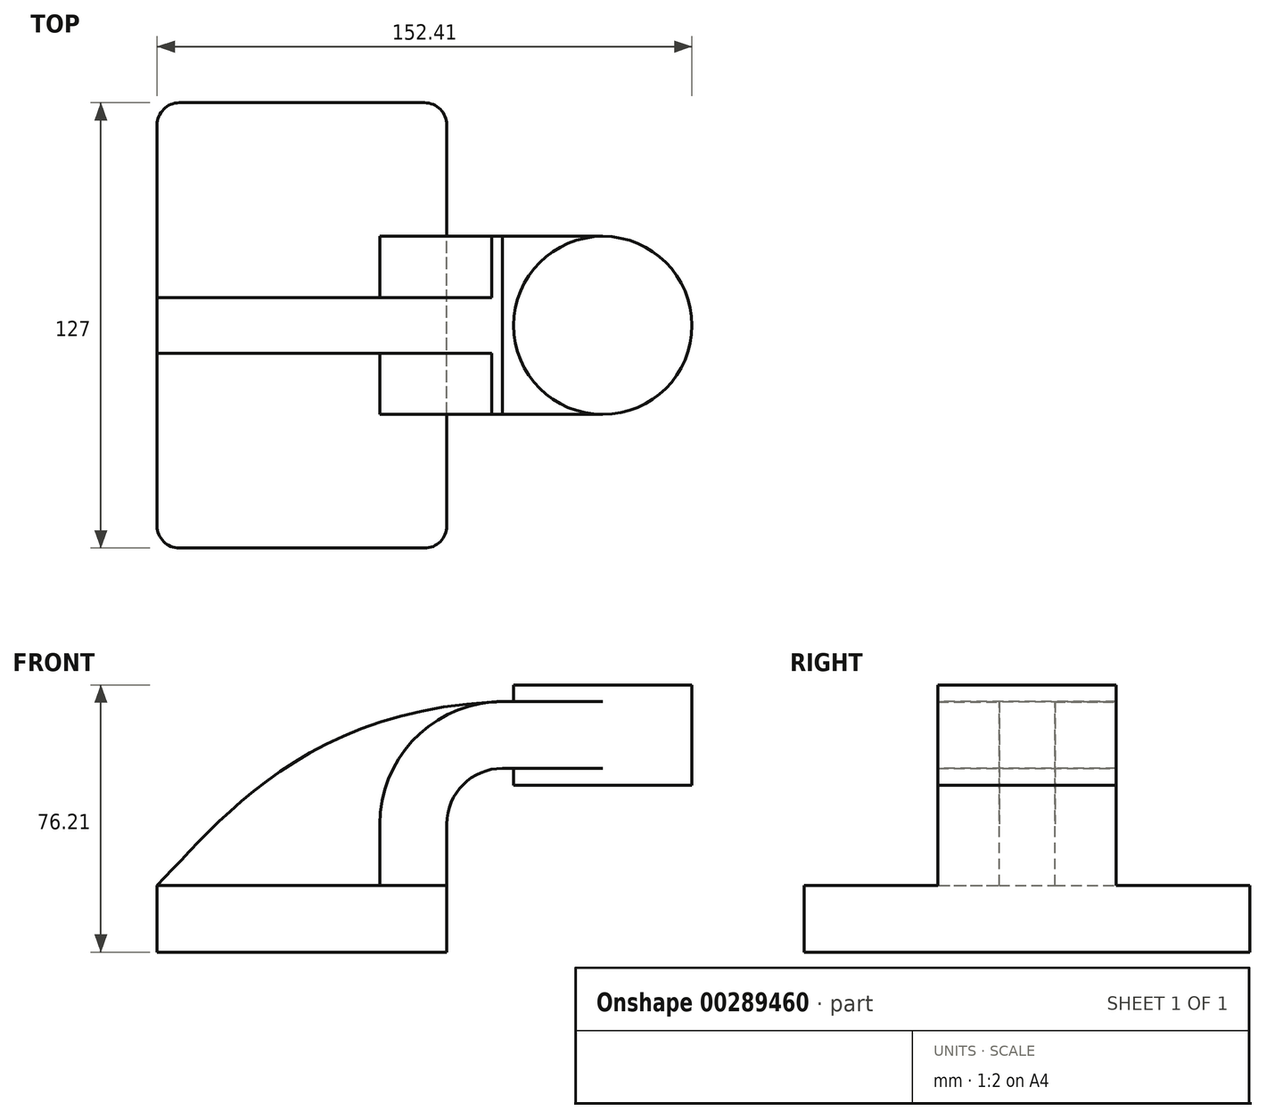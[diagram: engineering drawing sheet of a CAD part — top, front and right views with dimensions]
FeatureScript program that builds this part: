
annotation { "Feature Type Name" : "Feature", "Feature Type Description" : "" }
export const myFeature = defineFeature(function(context is Context, id is Id, definition is map)
    precondition{}
    {
        {
            var Q0;
            Q0=qCreatedBy(makeId("Front.planeOp"),FACE);
            var sketch = newSketch(context, id + "F0", { "sketchPlane" : qUnion([Q0])});
            skLineSegment(sketch, "E0.bottom", {"start": v(-41.28, -9.53) * mm, "end": v(41.28, -9.53) * mm});
            skLineSegment(sketch, "E0.top", {"start": v(-41.27, 9.53) * mm, "end": v(41.27, 9.53) * mm});
            skLineSegment(sketch, "E0.left", {"start": v(-41.28, -9.53) * mm, "end": v(-41.28, 9.52) * mm});
            skLineSegment(sketch, "E0.right", {"start": v(41.28, -9.53) * mm, "end": v(41.28, 9.52) * mm});
            skPoint(sketch, "E0.middle", {"position": v(0, 0) * mm});
            skLineSegment(sketch, "E1.bottom", {"start": v(60.33, 38.1) * mm, "end": v(111.12, 38.1) * mm});
            skLineSegment(sketch, "E1.top", {"start": v(60.32, 66.67) * mm, "end": v(111.12, 66.67) * mm});
            skLineSegment(sketch, "E1.left", {"start": v(60.33, 38.1) * mm, "end": v(60.32, 66.68) * mm});
            skLineSegment(sketch, "E1.right", {"start": v(111.12, 38.1) * mm, "end": v(111.12, 66.68) * mm});
            skPoint(sketch, "E1.middle", {"position": v(85.72, 52.39) * mm});
            skLineSegment(sketch, "E2", {"start": v(41.28, 9.52) * mm, "end": v(41.28, 27) * mm});
            skArc(sketch, "E3", {"start": v(41.28, 27) * mm, "mid": v(45.92, 38.23) * mm, "end": v(57.15, 42.88) * mm});
            skLineSegment(sketch, "E4", {"start": v(57.15, 42.88) * mm, "end": v(85.72, 42.88) * mm});
            skLineSegment(sketch, "E5.0", {"start": v(57.15, 61.93) * mm, "end": v(85.72, 61.93) * mm});
            skArc(sketch, "E5.1", {"start": v(22.23, 27) * mm, "mid": v(32.45, 51.7) * mm, "end": v(57.15, 61.93) * mm});
            skLineSegment(sketch, "E5.2", {"start": v(22.23, 9.52) * mm, "end": v(22.23, 27) * mm});
            skLineSegment(sketch, "E6", {"start": v(85.72, 66.67) * mm, "end": v(85.72, 38.1) * mm});
            skFitSpline(sketch, "E7", {"points": [v(-41.28, 9.52) * mm, v(57.15, 61.93) * mm], "startDerivative": vector(49.38, 49.75) * mm, "endDerivative": vector(171.45, 5.9) * mm});
            skSolve(sketch);
        }
        {
            var Q0;
            Q0=makeQuery(id+"F0.imprint","IMPRINT",FACE,{"disambiguationData":[TD([[makeQuery(id+"F0.imprint","IMPRINT",EDGE,{"derivedFrom":sQuery(id+"F0.wireOp",EDGE,"E0.bottom")}),1.0]])]});
            extrude(context, id + "F1", {"entities" : qUnion([Q0]), "endBound" : BoundingType.SYMMETRIC, "depth" : 127 * mm});
        }
        {
            var Q0;
            {var subQ1=sQuery(id+"F0.wireOp",EDGE,"E2");Q0=makeQuery(id+"F0.imprint","IMPRINT",FACE,{"disambiguationData":[TD([[makeQuery(id+"F0.imprint","IMPRINT",EDGE,{"derivedFrom":subQ1}),1.0]])]});}
            extrude(context, id + "F2", {"entities" : qUnion([Q0]), "operationType" : NewBodyOperationType.ADD, "endBound" : BoundingType.SYMMETRIC, "depth" : 50.8 * mm});
        }
        {
            var Q0;
            {var subQ0=sQuery(id+"F0.wireOp",EDGE,"E4");var subQ1=sQuery(id+"F0.wireOp",EDGE,"E1.left");var subQ2=makeQuery(id+"F0.imprint","INTERSECT",VERTEX,{"derivedFrom":[subQ1,subQ0]});Q0=makeQuery(id+"F0.imprint","IMPRINT",FACE,{"disambiguationData":[TD([[makeQuery(id+"F0.imprint","IMPRINT",EDGE,{"disambiguationData":[TD([[subQ2,-1.0]])],"derivedFrom":subQ1}),-1.0]])]});}
            extrude(context, id + "F3", {"entities" : qUnion([Q0]), "operationType" : NewBodyOperationType.ADD, "endBound" : BoundingType.SYMMETRIC, "depth" : 50.8 * mm});
        }
        {
            var Q0;
            {var subQ3=sQuery(id+"F0.wireOp",EDGE,"E5.2");Q0=makeQuery(id+"F0.imprint","IMPRINT",FACE,{"disambiguationData":[TD([[makeQuery(id+"F0.imprint","IMPRINT",EDGE,{"derivedFrom":subQ3}),1.0]])]});}
            extrude(context, id + "F4", {"entities" : qUnion([Q0]), "operationType" : NewBodyOperationType.ADD, "endBound" : BoundingType.SYMMETRIC, "depth" : 15.88 * mm});
        }
        {
            var Q0;
            {var subQ4=sQuery(id+"F0.wireOp",EDGE,"E1.right");Q0=makeQuery(id+"F0.imprint","IMPRINT",FACE,{"disambiguationData":[TD([[makeQuery(id+"F0.imprint","IMPRINT",EDGE,{"derivedFrom":subQ4}),1.0]])]});}
            var Q1;
            Q1=sQuery(id+"F0.wireOp",EDGE,"E6");
            revolve(context, id + "F5", {"operationType" : NewBodyOperationType.ADD, "entities" : qUnion([Q0]), "axis" : qUnion([Q1]), "revolveType" : RevolveType.FULL});
        }
        {
            var Q0;
            Q0=makeQuery(id+"F1.opExtrude","CAP_EDGE",EDGE,{"disambiguationData":[OSD([sQuery(id+"F0.wireOp",EDGE,"E0.right")])],"isStart":false});
            var Q1;
            Q1=makeQuery(id+"F1.opExtrude","CAP_EDGE",EDGE,{"disambiguationData":[OSD([sQuery(id+"F0.wireOp",EDGE,"E0.left")])],"isStart":false});
            var Q2;
            Q2=makeQuery(id+"F1.opExtrude","CAP_EDGE",EDGE,{"disambiguationData":[OSD([sQuery(id+"F0.wireOp",EDGE,"E0.right")])],"isStart":true});
            var Q3;
            Q3=makeQuery(id+"F1.opExtrude","CAP_EDGE",EDGE,{"disambiguationData":[OSD([sQuery(id+"F0.wireOp",EDGE,"E0.left")])],"isStart":true});
            fillet(context, id + "F6", {"entities" : qUnion([Q0, Q1, Q2, Q3]), "radius" : 6.35 * mm, "tangentPropagation" : true, "allowEdgeOverflow" : false});
        }
    });
